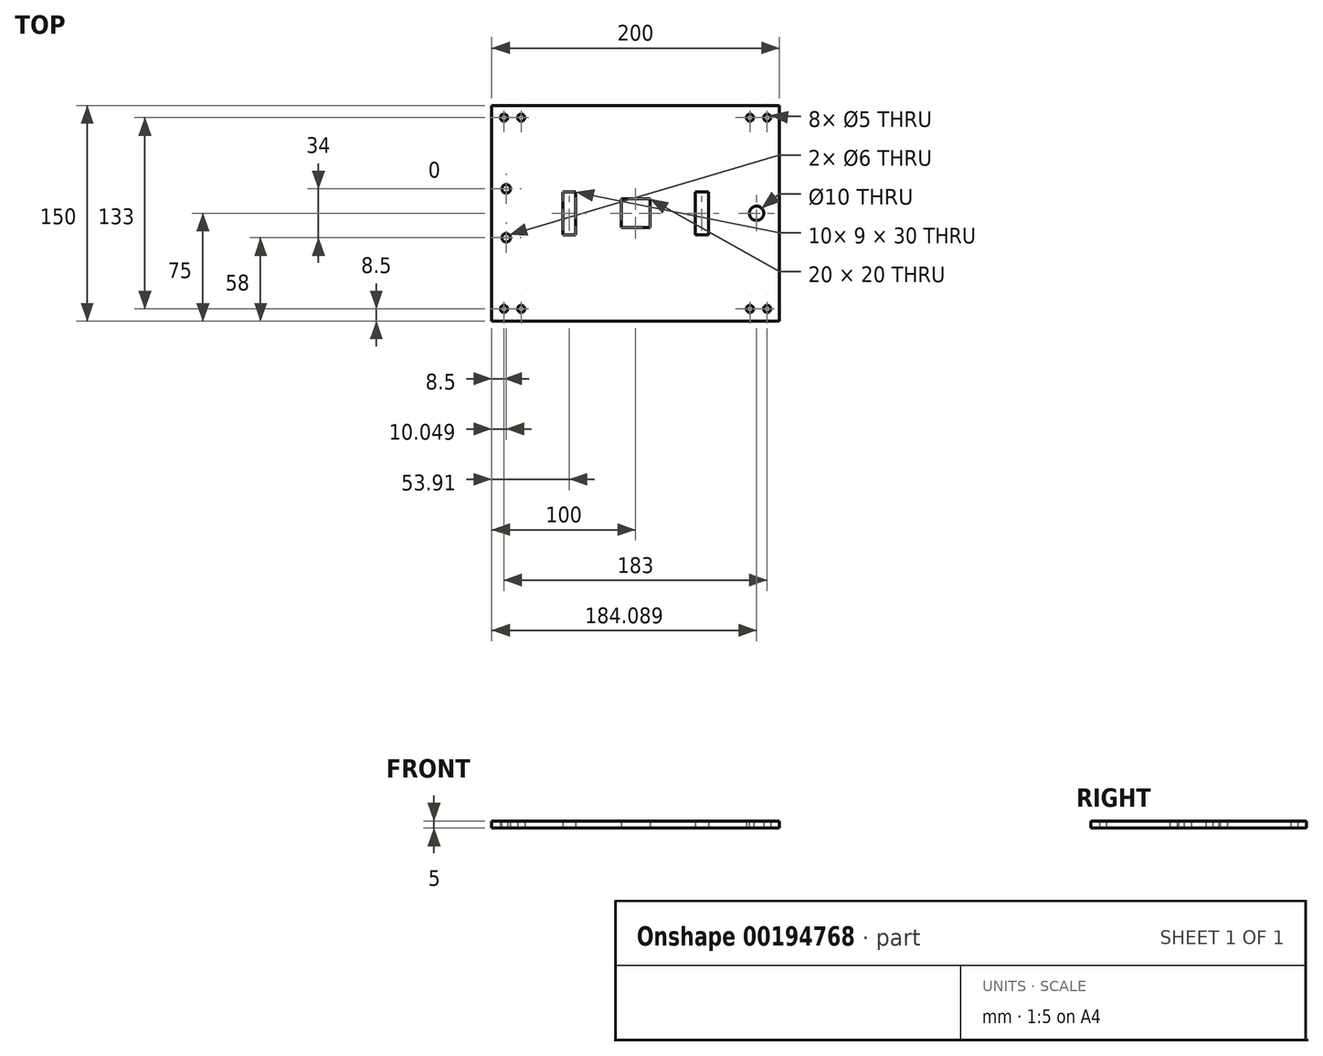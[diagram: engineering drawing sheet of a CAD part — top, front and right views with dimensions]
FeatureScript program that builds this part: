
annotation { "Feature Type Name" : "Feature", "Feature Type Description" : "" }
export const myFeature = defineFeature(function(context is Context, id is Id, definition is map)
    precondition{}
    {
        {
            var Q0;
            Q0=qCreatedBy(makeId("Top.planeOp"),FACE);
            var sketch = newSketch(context, id + "F0", { "sketchPlane" : qUnion([Q0])});
            skLineSegment(sketch, "E0.bottom", {"start": v(100, -75) * mm, "end": v(-100, -75) * mm});
            skLineSegment(sketch, "E0.top", {"start": v(100, 75) * mm, "end": v(-100, 75) * mm});
            skLineSegment(sketch, "E0.left", {"start": v(100, -75) * mm, "end": v(100, 75) * mm});
            skLineSegment(sketch, "E0.right", {"start": v(-100, -75) * mm, "end": v(-100, 75) * mm});
            skPoint(sketch, "E0.middle", {"position": v(0, 0) * mm});
            skLineSegment(sketch, "E1.bottom", {"start": v(-41.59, -15) * mm, "end": v(-50.59, -15) * mm});
            skLineSegment(sketch, "E1.top", {"start": v(-41.59, 15) * mm, "end": v(-50.59, 15) * mm});
            skLineSegment(sketch, "E1.left", {"start": v(-41.59, -15) * mm, "end": v(-41.59, 15) * mm});
            skLineSegment(sketch, "E1.right", {"start": v(-50.59, -15) * mm, "end": v(-50.59, 15) * mm});
            skPoint(sketch, "E1.middle", {"position": v(-46.09, 0) * mm});
            skLineSegment(sketch, "E2.MirrorCS", {"start": v(41.59, -15) * mm, "end": v(41.59, 15) * mm});
            skPoint(sketch, "E3.MirrorP", {"position": v(46.09, 0) * mm});
            skLineSegment(sketch, "E4.MirrorCS", {"start": v(50.59, -15) * mm, "end": v(50.59, 15) * mm});
            skLineSegment(sketch, "E5.MirrorCS", {"start": v(41.59, 15) * mm, "end": v(50.59, 15) * mm});
            skLineSegment(sketch, "E6.MirrorCS", {"start": v(41.59, -15) * mm, "end": v(50.59, -15) * mm});
            skSolve(sketch);
        }
        {
            var Q0;
            Q0=makeQuery(id+"F0.imprint","IMPRINT",FACE,{"disambiguationData":[TD([[makeQuery(id+"F0.imprint","IMPRINT",EDGE,{"derivedFrom":sQuery(id+"F0.wireOp",EDGE,"E0.bottom")}),-1.0]])]});
            var sketch = newSketch(context, id + "F1", { "sketchPlane" : qUnion([Q0])});
            skCircle(sketch, "E7", {"center": v(-91.5, 66.5) * mm, "radius": 2.5 * mm});
            skCircle(sketch, "E8.MirrorC", {"center": v(91.5, 66.5) * mm, "radius": 2.5 * mm});
            skCircle(sketch, "E9.MirrorC", {"center": v(-91.5, -66.5) * mm, "radius": 2.5 * mm});
            skCircle(sketch, "E10.MirrorC", {"center": v(91.5, -66.5) * mm, "radius": 2.5 * mm});
            skSolve(sketch);
        }
        {
            var Q0;
            Q0=makeQuery(id+"F0.imprint","IMPRINT",FACE,{"disambiguationData":[TD([[makeQuery(id+"F0.imprint","IMPRINT",EDGE,{"derivedFrom":sQuery(id+"F0.wireOp",EDGE,"E0.bottom")}),-1.0]])]});
            var sketch = newSketch(context, id + "F2", { "sketchPlane" : qUnion([Q0])});
            skCircle(sketch, "E11", {"center": v(-79.5, 66.5) * mm, "radius": 2.5 * mm});
            skCircle(sketch, "E12.MirrorC", {"center": v(79.5, 66.5) * mm, "radius": 2.5 * mm});
            skCircle(sketch, "E13.MirrorC", {"center": v(-79.5, -66.5) * mm, "radius": 2.5 * mm});
            skCircle(sketch, "E14.MirrorC", {"center": v(79.5, -66.5) * mm, "radius": 2.5 * mm});
            skSolve(sketch);
        }
        {
            var Q0;
            Q0=makeQuery(id+"F0.imprint","IMPRINT",FACE,{"disambiguationData":[TD([[makeQuery(id+"F0.imprint","IMPRINT",EDGE,{"derivedFrom":sQuery(id+"F0.wireOp",EDGE,"E0.bottom")}),-1.0]])]});
            var sketch = newSketch(context, id + "F3", { "sketchPlane" : qUnion([Q0])});
            skCircle(sketch, "E15", {"center": v(-89.95, 17) * mm, "radius": 3 * mm});
            skCircle(sketch, "E16.MirrorC", {"center": v(-89.95, -17) * mm, "radius": 3 * mm});
            skSolve(sketch);
        }
        {
            var Q0;
            Q0=makeQuery(id+"F0.imprint","IMPRINT",FACE,{"disambiguationData":[TD([[makeQuery(id+"F0.imprint","IMPRINT",EDGE,{"derivedFrom":sQuery(id+"F0.wireOp",EDGE,"E0.bottom")}),-1.0]])]});
            var sketch = newSketch(context, id + "F4", { "sketchPlane" : qUnion([Q0])});
            skLineSegment(sketch, "E17.bottom", {"start": v(10, -10) * mm, "end": v(-10, -10) * mm});
            skLineSegment(sketch, "E17.top", {"start": v(10, 10) * mm, "end": v(-10, 10) * mm});
            skLineSegment(sketch, "E17.left", {"start": v(10, -10) * mm, "end": v(10, 10) * mm});
            skLineSegment(sketch, "E17.right", {"start": v(-10, -10) * mm, "end": v(-10, 10) * mm});
            skPoint(sketch, "E17.middle", {"position": v(0, 0) * mm});
            skCircle(sketch, "E18", {"center": v(84.09, 0) * mm, "radius": 5 * mm});
            skSolve(sketch);
        }
        {
            var Q0;
            Q0=makeQuery(id+"F0.imprint","IMPRINT",FACE,{"disambiguationData":[TD([[makeQuery(id+"F0.imprint","IMPRINT",EDGE,{"derivedFrom":sQuery(id+"F0.wireOp",EDGE,"E0.bottom")}),-1.0]])]});
            var sketch = newSketch(context, id + "F5", { "sketchPlane" : qUnion([Q0])});
            skSolve(sketch);
        }
        {
            var Q0;
            Q0=makeQuery(id+"F0.imprint","IMPRINT",FACE,{"disambiguationData":[TD([[makeQuery(id+"F0.imprint","IMPRINT",EDGE,{"derivedFrom":sQuery(id+"F0.wireOp",EDGE,"E0.bottom")}),-1.0]])]});
            var Q1;
            Q1=makeQuery(id+"F1.imprint","IMPRINT",FACE,{"disambiguationData":[TD([[makeQuery(id+"F1.imprint","IMPRINT",EDGE,{"derivedFrom":sQuery(id+"F1.wireOp",EDGE,"E7")}),-1.0]])]});
            var Q2;
            Q2=makeQuery(id+"F2.imprint","IMPRINT",FACE,{"disambiguationData":[TD([[makeQuery(id+"F2.imprint","IMPRINT",EDGE,{"derivedFrom":sQuery(id+"F2.wireOp",EDGE,"E11")}),-1.0]])]});
            var Q3;
            Q3=makeQuery(id+"F5.imprint","IMPRINT",FACE,{"disambiguationData":[TD([[makeQuery(id+"F5.imprint","IMPRINT",EDGE,{"derivedFrom":makeQuery(id+"F0.imprint","IMPRINT",EDGE,{"derivedFrom":sQuery(id+"F0.wireOp",EDGE,"E0.bottom")})}),-1.0]])]});
            var Q4;
            Q4=makeQuery(id+"F4.imprint","IMPRINT",FACE,{"disambiguationData":[TD([[makeQuery(id+"F4.imprint","IMPRINT",EDGE,{"derivedFrom":sQuery(id+"F4.wireOp",EDGE,"E17.bottom")}),1.0]])]});
            var Q5;
            Q5=makeQuery(id+"F3.imprint","IMPRINT",FACE,{"disambiguationData":[TD([[makeQuery(id+"F3.imprint","IMPRINT",EDGE,{"derivedFrom":sQuery(id+"F3.wireOp",EDGE,"E15")}),-1.0]])]});
            extrude(context, id + "F6", {"entities" : qUnion([Q0, Q1, Q2, Q3, Q4, Q5]), "depth" : 5 * mm});
        }
    });
